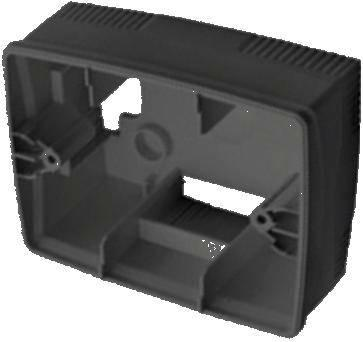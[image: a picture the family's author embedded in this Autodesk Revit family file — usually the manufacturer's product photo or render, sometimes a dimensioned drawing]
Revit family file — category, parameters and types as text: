
# Revit family: Domotics-DomesticRanges-GEWISS-CHORUS_BOX_WALLMOUNTING_BLACK
name_source: partatom
category: Apparecchi elettrici
revit_build: Autodesk Revit 2016 (Build: 20161004_0715(x64)
units: mm (PartAtom-declared; Revit-internal decimal feet)

## family parameters
Condiviso = No
Host = Superficie
Mantenere orientamento annotazione = No
Punto di calcolo locali = No
Quota connettore circolare = Usa diametro
Taglio con vuoti quando caricato = No
Tipo di parte = Normale

## types (2) — shared parameters
Altezza = 46 mm  [stored 0.150919 ft]
Catalogue = DOMOTICS
Catalogue Range = CHORUS - BOXES
Characteristics = Halogen free
Colour = Black
Electrocod = 0212
Glow Wire Test = 650 °C
Glow wire test: = 650 °C
IDF = 55992473-bd7b-47c4-8840-9d1075a56553
IDT = c93f3b70-7ef4-4ec4-9867-45809b3df11a
Immagine tipo = GW16774.jpg
Installation temperature = -5 +60 °C
Larghezza = 90 mm
Lunghezza = 140 mm
Material = Technopolymer
Produttore = GEWISS S.p.A.
Prospetto di default = 1219 mm
SEO = Box
Standard = EN 60670-1
Standard; = EN 60670-1
Suitable for plates = ONE
Technical sheet = https://www.gewiss.com
Thermo-pressure with ball = 70
Torque screws tightening = 0,8NM
URL = https://www.gewiss.com
Version file RFA = 18.0

## per-type parameters (varying)
| type | Description: | Descrizione | EAN code | Modello | Outer dim. LxHxD (mm) | Support |
| GW16773 - Wall box for one plates it st 3g black | 3 gang | WALL BOX FOR ONE PLATES IT ST 3G BLACK | 8011564278097 | GW16773 | 118x90x46 | GW16803 |
| GW16774 - Wall box for one plates it st 4g black | 4 gang | WALL BOX FOR ONE PLATES IT ST 4G BLACK | 8011564279377 | GW16774 | 140x90x46 | GW16804 |

note: source unit labels omitted for Thermo-pressure with ball — the stored unit's dimension contradicts the parameter name (converter mislabeling)

note: [stored X ft] marks values corroborated as IEEE doubles in the binary element streams (Revit-internal decimal feet)

## geometry (parser evidence)
native form markers: Blend x4
no freeform markers — native parametric forms only
